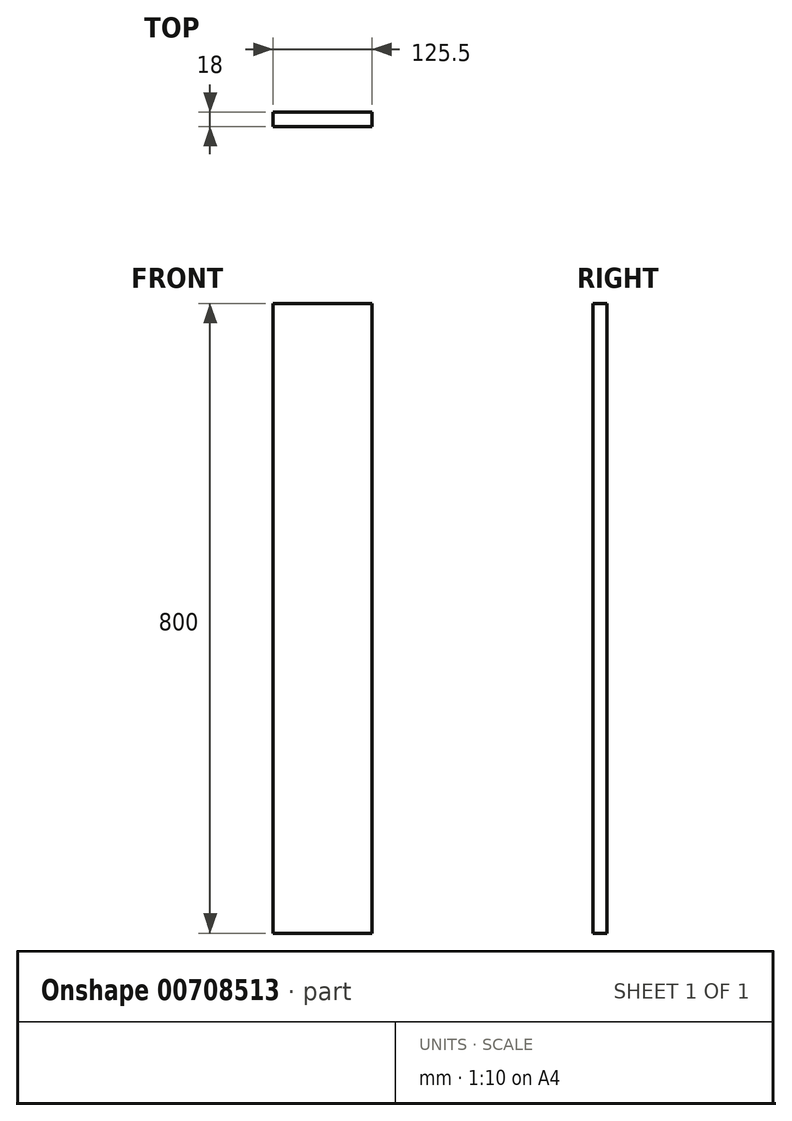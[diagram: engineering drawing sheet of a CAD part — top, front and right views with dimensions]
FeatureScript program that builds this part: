
annotation { "Feature Type Name" : "Feature", "Feature Type Description" : "" }
export const myFeature = defineFeature(function(context is Context, id is Id, definition is map)
    precondition{}
    {
        {
            var Q0;
            Q0=qCreatedBy(makeId("Front.planeOp"),FACE);
            var sketch = newSketch(context, id + "F0", { "sketchPlane" : qUnion([Q0])});
            skLineSegment(sketch, "E0.bottom", {"start": v(0, 0) * mm, "end": v(125.5, 0) * mm});
            skLineSegment(sketch, "E0.top", {"start": v(0, -800) * mm, "end": v(125.5, -800) * mm});
            skLineSegment(sketch, "E0.left", {"start": v(0, 0) * mm, "end": v(0, -800) * mm});
            skLineSegment(sketch, "E0.right", {"start": v(125.5, 0) * mm, "end": v(125.5, -800) * mm});
            skSolve(sketch);
        }
        {
            var Q0;
            Q0=qSketchRegion(id+"F0",true);
            extrude(context, id + "F1", {"entities" : qUnion([Q0]), "oppositeDirection" : true, "depth" : 18 * mm, "offsetDistance" : 25 * mm});
        }
    });
